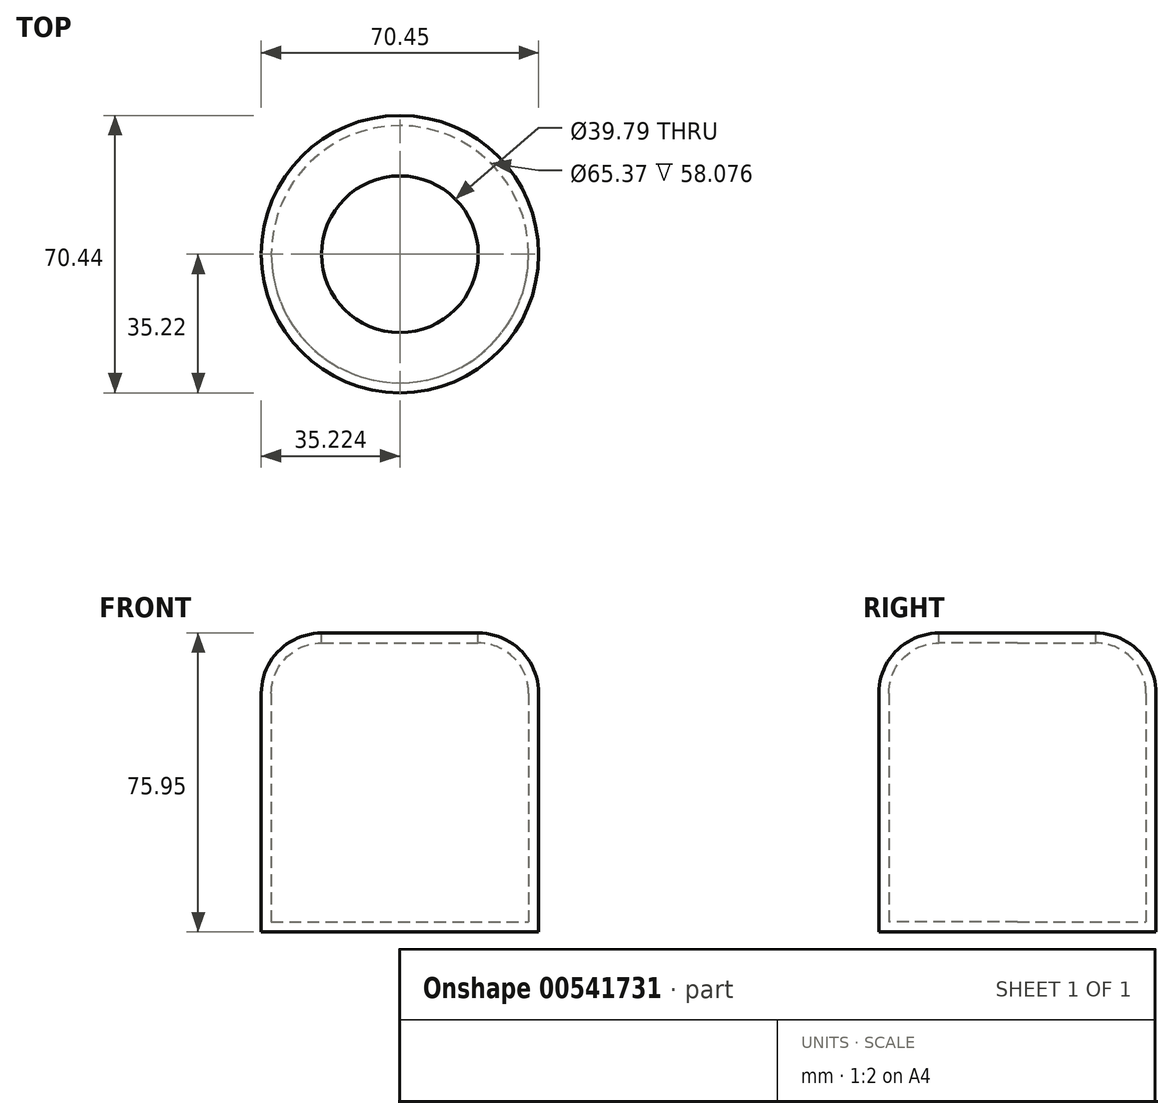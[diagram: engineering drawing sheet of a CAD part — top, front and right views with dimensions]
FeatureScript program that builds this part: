
annotation { "Feature Type Name" : "Feature", "Feature Type Description" : "" }
export const myFeature = defineFeature(function(context is Context, id is Id, definition is map)
    precondition{}
    {
        {
            var Q0;
            Q0=qCreatedBy(makeId("Top.planeOp"),FACE);
            var sketch = newSketch(context, id + "F0", { "sketchPlane" : qUnion([Q0])});
            skLineSegment(sketch, "E0", {"start": v(-131.64, 0) * mm, "end": v(-131.64, 37.4) * mm});
            skLineSegment(sketch, "E1", {"start": v(-131.64, 37.4) * mm, "end": v(-75.98, 37.4) * mm});
            skLineSegment(sketch, "E2", {"start": v(-75.98, 37.4) * mm, "end": v(-61.2, 0) * mm});
            skArc(sketch, "E3", {"start": v(-131.64, 0) * mm, "mid": v(-96.42, -35.22) * mm, "end": v(-61.2, 0) * mm});
            skCircle(sketch, "E4", {"center": v(-4.9, -47.14) * mm, "radius": 35.22 * mm});
            skSolve(sketch);
        }
        {
            var Q0;
            Q0=makeQuery(id+"F0.imprint","IMPRINT",FACE,{"disambiguationData":[TD([[makeQuery(id+"F0.imprint","IMPRINT",EDGE,{"derivedFrom":sQuery(id+"F0.wireOp",EDGE,"E4")}),1.0]])]});
            extrude(context, id + "F1", {"entities" : qUnion([Q0]), "depth" : 75.95 * mm, "offsetDistance" : 25.4 * mm});
        }
        {
            var Q0;
            Q0=makeQuery(id+"F1.opExtrude","CAP_EDGE",EDGE,{"disambiguationData":[OSD([sQuery(id+"F0.wireOp",EDGE,"E4")])],"isStart":false});
            fillet(context, id + "F2", {"entities" : qUnion([Q0]), "radius" : 15.33 * mm, "tangentPropagation" : true, "allowEdgeOverflow" : false});
        }
        {
            var Q0;
            Q0=makeQuery(id+"F1.opExtrude","CAP_FACE",FACE,{"disambiguationData":[OSD([sQuery(id+"F0.wireOp",EDGE,"E4")])],"isStart":false});
            shell(context, id + "F3", {"entities" : qUnion([Q0]), "thickness" : 2.54 * mm});
        }
    });
